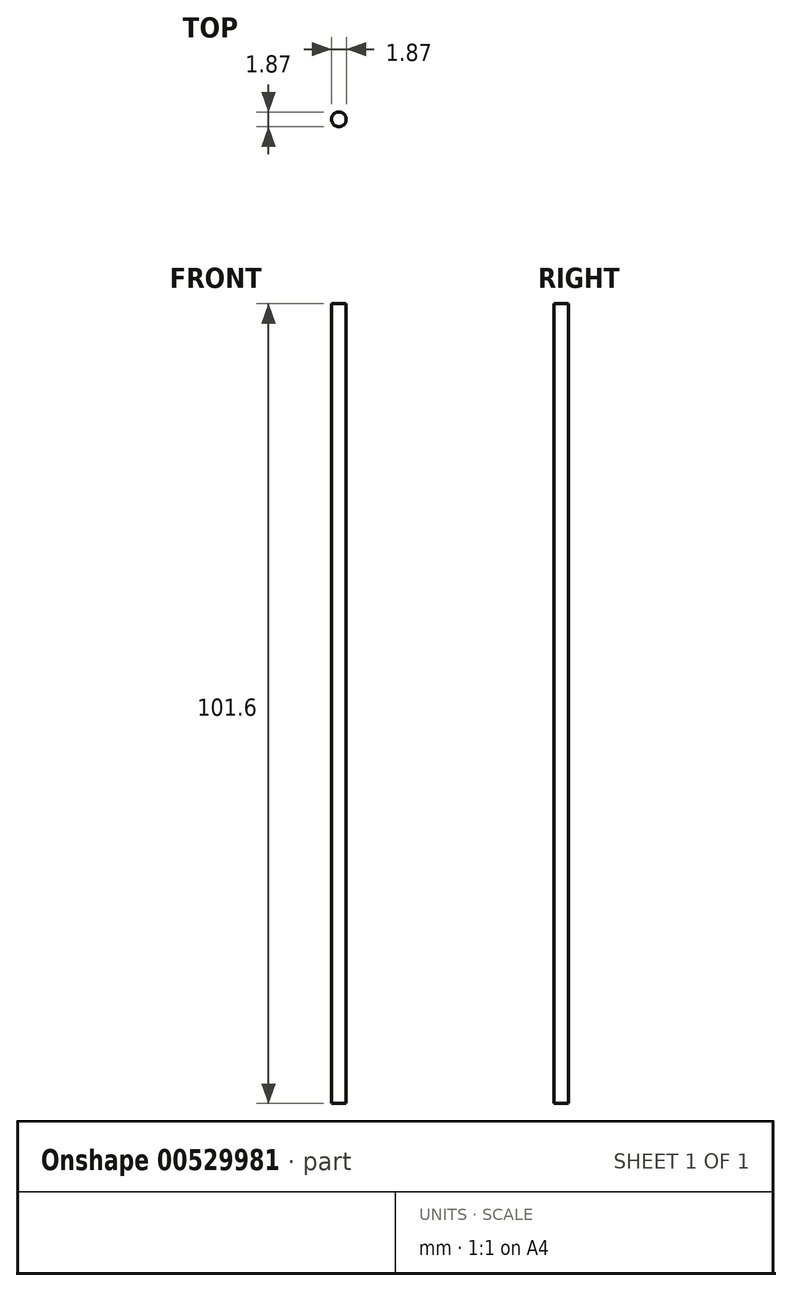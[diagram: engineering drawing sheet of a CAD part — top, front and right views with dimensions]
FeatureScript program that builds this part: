
annotation { "Feature Type Name" : "Feature", "Feature Type Description" : "" }
export const myFeature = defineFeature(function(context is Context, id is Id, definition is map)
    precondition{}
    {
        {
            var Q0;
            Q0=qCreatedBy(makeId("Top.planeOp"),FACE);
            var sketch = newSketch(context, id + "F0", { "sketchPlane" : qUnion([Q0])});
            skCircle(sketch, "E0", {"center": v(-28.05, 17.71) * mm, "radius": 0.93 * mm});
            skSolve(sketch);
        }
        {
            var Q0;
            Q0=makeQuery(id+"F0.imprint","IMPRINT",FACE,{"disambiguationData":[TD([[makeQuery(id+"F0.imprint","IMPRINT",EDGE,{"derivedFrom":sQuery(id+"F0.wireOp",EDGE,"E0")}),1.0]])]});
            extrude(context, id + "F1", {"entities" : qUnion([Q0]), "depth" : 101.6 * mm, "offsetDistance" : 25.4 * mm});
        }
    });
